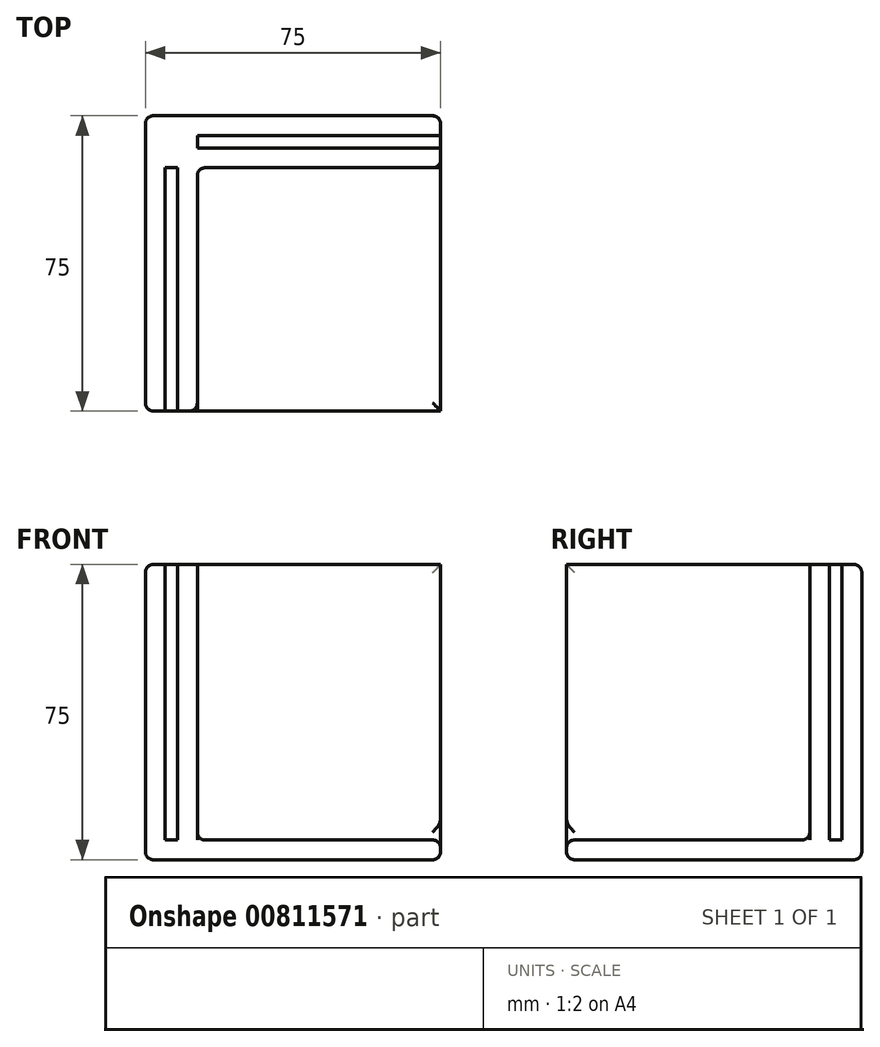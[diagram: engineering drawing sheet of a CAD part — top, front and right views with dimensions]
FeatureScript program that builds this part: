
annotation { "Feature Type Name" : "Feature", "Feature Type Description" : "" }
export const myFeature = defineFeature(function(context is Context, id is Id, definition is map)
    precondition{}
    {
        {
            var Q0;
            Q0=qCreatedBy(makeId("Top.planeOp"),FACE);
            var sketch = newSketch(context, id + "F0", { "sketchPlane" : qUnion([Q0])});
            skLineSegment(sketch, "E0.bottom", {"start": v(37.5, -37.5) * mm, "end": v(-37.5, -37.5) * mm});
            skLineSegment(sketch, "E0.top", {"start": v(37.5, 37.5) * mm, "end": v(-37.5, 37.5) * mm});
            skLineSegment(sketch, "E0.left", {"start": v(37.5, -37.5) * mm, "end": v(37.5, 37.5) * mm});
            skLineSegment(sketch, "E0.right", {"start": v(-37.5, -37.5) * mm, "end": v(-37.5, 37.5) * mm});
            skPoint(sketch, "E0.middle", {"position": v(0, 0) * mm});
            skSolve(sketch);
        }
        {
            var Q0;
            Q0 = qSketchRegion(id + "F0", true);
            extrude(context, id + "F1", {"entities" : qUnion([Q0]), "depth" : 5 * mm, "offsetDistance" : 25 * mm});
        }
        {
            var Q0;
            Q0=makeQuery(id+"F1.opExtrude","CAP_FACE",FACE,{"disambiguationData":[OSD([sQuery(id+"F0.wireOp",EDGE,"E0.bottom"),sQuery(id+"F0.wireOp",EDGE,"E0.top"),sQuery(id+"F0.wireOp",EDGE,"E0.left"),sQuery(id+"F0.wireOp",EDGE,"E0.right")])],"isStart":false});
            var sketch = newSketch(context, id + "F2", { "sketchPlane" : qUnion([Q0])});
            skLineSegment(sketch, "E1.bottom", {"start": v(-37.5, 37.5) * mm, "end": v(-32.5, 37.5) * mm});
            skLineSegment(sketch, "E1.top", {"start": v(-37.5, -37.5) * mm, "end": v(-32.5, -37.5) * mm});
            skLineSegment(sketch, "E1.left", {"start": v(-37.5, 37.5) * mm, "end": v(-37.5, -37.5) * mm});
            skLineSegment(sketch, "E1.right", {"start": v(-32.5, 37.5) * mm, "end": v(-32.5, -37.5) * mm});
            skLineSegment(sketch, "E2.bottom", {"start": v(37.5, 37.5) * mm, "end": v(-37.5, 37.5) * mm});
            skLineSegment(sketch, "E2.top", {"start": v(37.5, 32.5) * mm, "end": v(-37.5, 32.5) * mm});
            skLineSegment(sketch, "E2.left", {"start": v(37.5, 37.5) * mm, "end": v(37.5, 32.5) * mm});
            skLineSegment(sketch, "E2.right", {"start": v(-37.5, 37.5) * mm, "end": v(-37.5, 32.5) * mm});
            skLineSegment(sketch, "E3.bottom", {"start": v(-29.3, 37.5) * mm, "end": v(-24.3, 37.5) * mm});
            skLineSegment(sketch, "E3.top", {"start": v(-29.3, -37.5) * mm, "end": v(-24.3, -37.5) * mm});
            skLineSegment(sketch, "E3.left", {"start": v(-29.3, 37.5) * mm, "end": v(-29.3, -37.5) * mm});
            skLineSegment(sketch, "E3.right", {"start": v(-24.3, 37.5) * mm, "end": v(-24.3, -37.5) * mm});
            skLineSegment(sketch, "E4.bottom", {"start": v(-37.5, 29.3) * mm, "end": v(37.5, 29.3) * mm});
            skLineSegment(sketch, "E4.top", {"start": v(-37.5, 24.3) * mm, "end": v(37.5, 24.3) * mm});
            skLineSegment(sketch, "E4.left", {"start": v(-37.5, 29.3) * mm, "end": v(-37.5, 24.3) * mm});
            skLineSegment(sketch, "E4.right", {"start": v(37.5, 29.3) * mm, "end": v(37.5, 24.3) * mm});
            skSolve(sketch);
        }
        {
            var Q0;
            Q0 = qSketchRegion(id + "F2", true);
            extrude(context, id + "F3", {"entities" : qUnion([Q0]), "operationType" : NewBodyOperationType.ADD, "depth" : 70 * mm, "offsetDistance" : 25 * mm});
        }
        {
            var Q0;
            Q0=makeQuery(id+"F1.opExtrude","CAP_FACE",FACE,{"disambiguationData":[OSD([sQuery(id+"F0.wireOp",EDGE,"E0.bottom"),sQuery(id+"F0.wireOp",EDGE,"E0.top"),sQuery(id+"F0.wireOp",EDGE,"E0.left"),sQuery(id+"F0.wireOp",EDGE,"E0.right")])],"isStart":true});
            var Q1;
            Q1=makeQuery(id+"F3.boolean.opBoolean","MERGE",FACE,{"derivedFrom":[makeQuery(id+"F1.opExtrude","SWEPT_FACE",FACE,{"disambiguationData":[OSD([sQuery(id+"F0.wireOp",EDGE,"E0.right")])]}),makeQuery(id+"F3.opExtrude","SWEPT_FACE",FACE,{"disambiguationData":[OSD([sQuery(id+"F2.wireOp",EDGE,"M5YcsCfr-pvcU-yWks-6ihz-tbSOXkpsQLRh.left")])]})]});
            var Q2;
            Q2=makeQuery(id+"F3.boolean.opBoolean","MERGE",FACE,{"derivedFrom":[makeQuery(id+"F1.opExtrude","SWEPT_FACE",FACE,{"disambiguationData":[OSD([sQuery(id+"F0.wireOp",EDGE,"E0.top")])]}),makeQuery(id+"F3.opExtrude","SWEPT_FACE",FACE,{"disambiguationData":[OSD([sQuery(id+"F2.wireOp",EDGE,"M5YcsCfr-pvcU-yWks-6ihz-tbSOXkpsQLRh.top"),sQuery(id+"F2.wireOp",EDGE,"3u02SwK4-xcQg-xW4M-OONb-UyZOXjzJWRte.top")])]})]});
            var Q3;
            {var subQ0=sQuery(id+"F0.wireOp",EDGE,"E0.left");var subQ1=sQuery(id+"F0.wireOp",EDGE,"E0.bottom");Q3=makeQuery(id+"F3.boolean.opBoolean","SPLIT",FACE,{"disambiguationData":[TD([makeQuery(id+"F3.opExtrude","SWEPT_FACE",FACE,{"disambiguationData":[OSD([sQuery(id+"F2.wireOp",EDGE,"U4OE86xM-2nj9-5kqX-hZhN-euJrliqOmqsM.right")])]})])],"derivedFrom":makeQuery(id+"F1.opExtrude","CAP_FACE",FACE,{"disambiguationData":[OSD([subQ1,sQuery(id+"F0.wireOp",EDGE,"E0.top"),subQ0,sQuery(id+"F0.wireOp",EDGE,"E0.right")])],"isStart":false})});}
            var Q4;
            Q4=makeQuery(id+"F3.opExtrude","SWEPT_EDGE",EDGE,{"disambiguationData":[OSD([sQuery(id+"F2.wireOp",EDGE,"U4OE86xM-2nj9-5kqX-hZhN-euJrliqOmqsM.right"),sQuery(id+"F2.wireOp",EDGE,"hKQ6JI1m-YdC8-uINN-MBrZ-ORUy9FCE7vJ7.top"),sQuery(id+"F2.wireOp",EDGE,"hKQ6JI1m-YdC8-uINN-MBrZ-ORUy9FCE7vJ7.left")])]});
            var Q5;
            Q5=makeQuery(id+"F3.opExtrude","SWEPT_EDGE",EDGE,{"disambiguationData":[OSD([sQuery(id+"F2.wireOp",EDGE,"E3.right"),sQuery(id+"F2.wireOp",EDGE,"E4.top")])]});
            var Q6;
            {var subQ0=sQuery(id+"F2.wireOp",EDGE,"E4.top");Q6=makeQuery(id+"F3.opExtrude","CAP_EDGE",EDGE,{"disambiguationData":[OSD([subQ0]),TDD([makeQuery(id+"F2.imprint","IMPRINT",EDGE,{"disambiguationData":[TD([[makeQuery(id+"F2.imprint","INTERSECT",VERTEX,{"derivedFrom":[sQuery(id+"F2.wireOp",EDGE,"E3.right"),subQ0]}),-1.0]])],"derivedFrom":subQ0})])],"isStart":true});}
            var Q7;
            {var subQ0=sQuery(id+"F2.wireOp",EDGE,"E3.right");Q7=makeQuery(id+"F3.opExtrude","CAP_EDGE",EDGE,{"disambiguationData":[OSD([subQ0]),TDD([makeQuery(id+"F2.imprint","IMPRINT",EDGE,{"disambiguationData":[TD([[makeQuery(id+"F2.imprint","INTERSECT",VERTEX,{"derivedFrom":[subQ0,sQuery(id+"F2.wireOp",EDGE,"E4.top")]}),-1.0]])],"derivedFrom":subQ0})])],"isStart":true});}
            var Q8;
            {var subQ0=sQuery(id+"F0.wireOp",EDGE,"E0.left");var subQ1=sQuery(id+"F2.wireOp",EDGE,"E3.right");var subQ3=sQuery(id+"F0.wireOp",EDGE,"E0.bottom");var subQ4=sQuery(id+"F2.wireOp",EDGE,"E4.top");var subQ5=makeQuery(id+"F2.imprint","INTERSECT",VERTEX,{"derivedFrom":[subQ1,subQ4]});Q8=makeQuery(id+"F3.boolean.opBoolean","SPLIT",FACE,{"disambiguationData":[TD([makeQuery(id+"F3.opExtrude","SWEPT_FACE",FACE,{"disambiguationData":[OSD([subQ1]),TDD([makeQuery(id+"F2.imprint","IMPRINT",EDGE,{"disambiguationData":[TD([[subQ5,-1.0]])],"derivedFrom":subQ1})])]})])],"derivedFrom":makeQuery(id+"F1.opExtrude","CAP_FACE",FACE,{"disambiguationData":[OSD([subQ3,sQuery(id+"F0.wireOp",EDGE,"E0.top"),subQ0,sQuery(id+"F0.wireOp",EDGE,"E0.right")])],"isStart":false})});}
            fillet(context, id + "F4", {"entities" : qUnion([Q0, Q1, Q2, Q3, Q4, Q5, Q6, Q7, Q8]), "radius" : 2 * mm, "tangentPropagation" : true, "allowEdgeOverflow" : false});
        }
        {
            var Q0;
            Q0=makeQuery(id+"F3.opExtrude","CAP_FACE",FACE,{"disambiguationData":[OSD([sQuery(id+"F2.wireOp",EDGE,"E1.top"),sQuery(id+"F2.wireOp",EDGE,"E1.left"),sQuery(id+"F2.wireOp",EDGE,"E1.right"),sQuery(id+"F2.wireOp",EDGE,"E2.bottom"),sQuery(id+"F2.wireOp",EDGE,"E2.top"),sQuery(id+"F2.wireOp",EDGE,"E2.left"),sQuery(id+"F2.wireOp",EDGE,"E2.right"),sQuery(id+"F2.wireOp",EDGE,"E3.bottom"),sQuery(id+"F2.wireOp",EDGE,"E3.top"),sQuery(id+"F2.wireOp",EDGE,"E3.left"),sQuery(id+"F2.wireOp",EDGE,"E3.right"),sQuery(id+"F2.wireOp",EDGE,"E4.bottom"),sQuery(id+"F2.wireOp",EDGE,"E4.top"),sQuery(id+"F2.wireOp",EDGE,"E4.left"),sQuery(id+"F2.wireOp",EDGE,"E4.right")])],"isStart":false});
            var sketch = newSketch(context, id + "F5", { "sketchPlane" : qUnion([Q0])});
            skLineSegment(sketch, "E5.bottom", {"start": v(-32.5, 32.5) * mm, "end": v(-29.3, 32.5) * mm});
            skLineSegment(sketch, "E5.top", {"start": v(-32.5, 29.3) * mm, "end": v(-29.3, 29.3) * mm});
            skLineSegment(sketch, "E5.left", {"start": v(-32.5, 32.5) * mm, "end": v(-32.5, 29.3) * mm});
            skLineSegment(sketch, "E5.right", {"start": v(-29.3, 32.5) * mm, "end": v(-29.3, 29.3) * mm});
            skSolve(sketch);
        }
        {
            var Q0;
            Q0 = qSketchRegion(id + "F5", true);
            var Q1;
            Q1=makeQuery(id+"F1.opExtrude","CAP_FACE",FACE,{"disambiguationData":[OSD([sQuery(id+"F0.wireOp",EDGE,"E0.bottom"),sQuery(id+"F0.wireOp",EDGE,"E0.top"),sQuery(id+"F0.wireOp",EDGE,"E0.left"),sQuery(id+"F0.wireOp",EDGE,"E0.right")])],"isStart":true});
            extrude(context, id + "F6", {"entities" : qUnion([Q0]), "operationType" : NewBodyOperationType.ADD, "endBound" : BoundingType.UP_TO_SURFACE, "oppositeDirection" : true, "depth" : 25 * mm, "endBoundEntityFace" : qUnion([Q1]), "offsetDistance" : 25 * mm});
        }
    });
